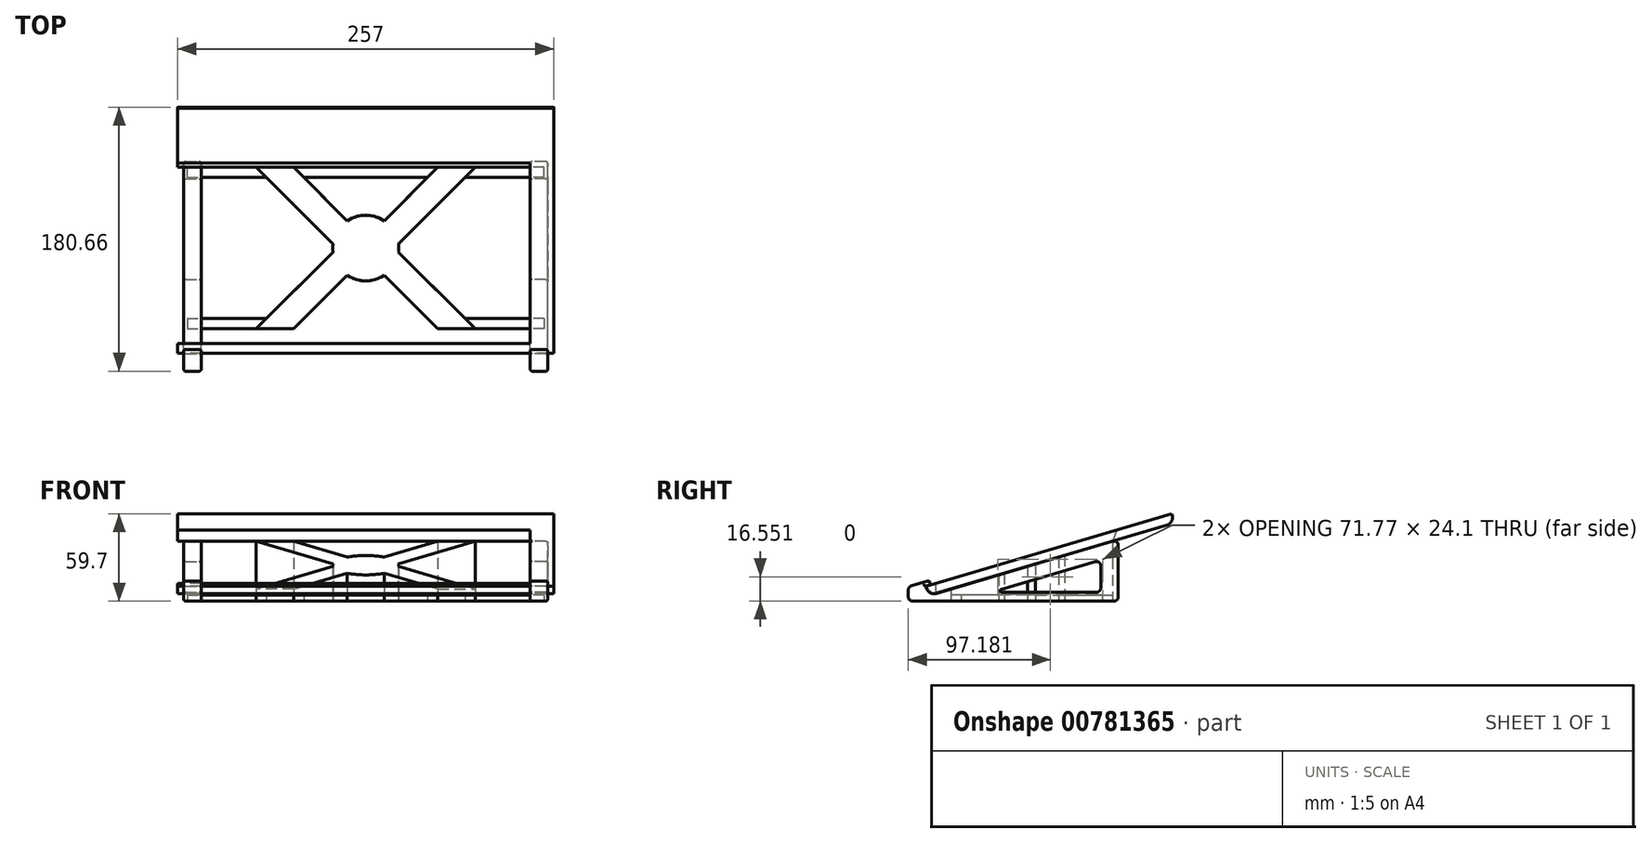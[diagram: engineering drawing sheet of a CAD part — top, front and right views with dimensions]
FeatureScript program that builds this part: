
annotation { "Feature Type Name" : "Feature", "Feature Type Description" : "" }
export const myFeature = defineFeature(function(context is Context, id is Id, definition is map)
    precondition{}
    {
        {
            var Q0;
            Q0=qCreatedBy(makeId("Right.planeOp"),FACE);
            var sketch = newSketch(context, id + "F0", { "sketchPlane" : qUnion([Q0])});
            skLineSegment(sketch, "E0", {"start": v(0, 10) * mm, "end": v(167.8, 59.7) * mm});
            skLineSegment(sketch, "E1", {"start": v(167.8, 59.7) * mm, "end": v(168.16, 58.46) * mm});
            skLineSegment(sketch, "E2", {"start": v(164.65, 52) * mm, "end": v(6.83, 5.24) * mm});
            skLineSegment(sketch, "E3", {"start": v(0.37, 8.75) * mm, "end": v(0, 10) * mm});
            skPoint(sketch, "E4.visualSharp", {"position": v(1.85, 3.77) * mm});
            skArc(sketch, "E4.filletArc", {"start": v(0.37, 8.75) * mm, "mid": v(2.87, 5.66) * mm, "end": v(6.83, 5.24) * mm});
            skPoint(sketch, "E5.visualSharp", {"position": v(169.64, 53.47) * mm});
            skArc(sketch, "E5.filletArc", {"start": v(164.65, 52) * mm, "mid": v(167.75, 54.5) * mm, "end": v(168.16, 58.46) * mm});
            skLineSegment(sketch, "E6", {"start": v(0, 0) * mm, "end": v(83.66, 0) * mm, "construction": true});
            skSolve(sketch);
        }
        {
            var Q0;
            Q0=makeQuery(id+"F0.imprint","IMPRINT",FACE,{"disambiguationData":[TD([[makeQuery(id+"F0.imprint","IMPRINT",EDGE,{"derivedFrom":sQuery(id+"F0.wireOp",EDGE,"E0")}),-1.0]])]});
            extrude(context, id + "F1", {"entities" : qUnion([Q0]), "endBound" : BoundingType.SYMMETRIC, "depth" : 257 * mm, "offsetDistance" : 25 * mm});
        }
        {
            var Q0;
            Q0=makeQuery(id+"F1.opExtrude","CAP_FACE",FACE,{"disambiguationData":[OSD([sQuery(id+"F0.wireOp",EDGE,"E0"),sQuery(id+"F0.wireOp",EDGE,"E1"),sQuery(id+"F0.wireOp",EDGE,"E2"),sQuery(id+"F0.wireOp",EDGE,"E3"),sQuery(id+"F0.wireOp",EDGE,"E4.filletArc"),sQuery(id+"F0.wireOp",EDGE,"E5.filletArc")])],"isStart":false});
            cPlane(context, id + "F2", {"entities" : qUnion([Q0]), "cplaneType" : CPlaneType.OFFSET, "offset" : 16 * mm, "oppositeDirection" : true, "width" : 150 * mm, "height" : 150 * mm});
        }
        {
            var Q0;
            Q0=qCreatedBy(id+"F2.planeOp",FACE);
            var sketch = newSketch(context, id + "F3", { "sketchPlane" : qUnion([Q0])});
            skLineSegment(sketch, "E7", {"start": v(6.74, 5.22) * mm, "end": v(127.43, 40.97) * mm});
            skLineSegment(sketch, "E8", {"start": v(131.29, 38.1) * mm, "end": v(131.29, 3) * mm});
            skLineSegment(sketch, "E9", {"start": v(-9.28, 0) * mm, "end": v(128.29, 0) * mm});
            skLineSegment(sketch, "E10.0", {"start": v(167.8, 59.7) * mm, "end": v(168.16, 58.46) * mm, "construction": true});
            skLineSegment(sketch, "E11", {"start": v(131.29, 42.1) * mm, "end": v(169.64, 53.47) * mm, "construction": true});
            skLineSegment(sketch, "E12", {"start": v(169.64, 53.47) * mm, "end": v(168.16, 58.46) * mm, "construction": true});
            skArc(sketch, "E13", {"start": v(6.74, 5.22) * mm, "mid": v(2.7, 5.64) * mm, "end": v(0.15, 8.8) * mm});
            skLineSegment(sketch, "E14", {"start": v(-0.28, 10.23) * mm, "end": v(0.15, 8.8) * mm});
            skLineSegment(sketch, "E15.0", {"start": v(0, 10) * mm, "end": v(167.8, 59.7) * mm, "construction": true});
            skLineSegment(sketch, "E16", {"start": v(-0.28, 10.23) * mm, "end": v(1.64, 10.8) * mm});
            skLineSegment(sketch, "E17", {"start": v(-12.28, 7.56) * mm, "end": v(-12.28, 3) * mm});
            skLineSegment(sketch, "E18", {"start": v(0.79, 13.68) * mm, "end": v(-10.13, 10.44) * mm});
            skArc(sketch, "E19", {"start": v(0.79, 13.68) * mm, "mid": v(2.65, 12.66) * mm, "end": v(1.64, 10.8) * mm});
            skLineSegment(sketch, "E20", {"start": v(51.2, 7.96) * mm, "end": v(115.43, 26.98) * mm});
            skLineSegment(sketch, "E21", {"start": v(119.29, 24.1) * mm, "end": v(119.29, 9) * mm});
            skLineSegment(sketch, "E22", {"start": v(116.29, 6) * mm, "end": v(51.49, 6) * mm});
            skPoint(sketch, "E23.visualSharp", {"position": v(44.6, 6) * mm});
            skArc(sketch, "E23.filletArc", {"start": v(51.2, 7.96) * mm, "mid": v(50.5, 6.86) * mm, "end": v(51.49, 6) * mm});
            skPoint(sketch, "E24.visualSharp", {"position": v(119.29, 28.13) * mm});
            skArc(sketch, "E24.filletArc", {"start": v(119.29, 24.1) * mm, "mid": v(118.08, 26.51) * mm, "end": v(115.43, 26.98) * mm});
            skPoint(sketch, "E25.visualSharp", {"position": v(119.29, 6) * mm});
            skArc(sketch, "E25.filletArc", {"start": v(116.29, 6) * mm, "mid": v(118.4, 6.88) * mm, "end": v(119.29, 9) * mm});
            skPoint(sketch, "E26.visualSharp", {"position": v(131.29, 0) * mm});
            skArc(sketch, "E26.filletArc", {"start": v(128.29, 0) * mm, "mid": v(130.4, 0.88) * mm, "end": v(131.29, 3) * mm});
            skPoint(sketch, "E27.visualSharp", {"position": v(131.29, 42.1) * mm});
            skArc(sketch, "E27.filletArc", {"start": v(131.29, 38.1) * mm, "mid": v(130.08, 40.5) * mm, "end": v(127.43, 40.97) * mm});
            skPoint(sketch, "E28.visualSharp", {"position": v(-12.28, 0) * mm});
            skArc(sketch, "E28.filletArc", {"start": v(-12.28, 3) * mm, "mid": v(-11.4, 0.88) * mm, "end": v(-9.28, 0) * mm});
            skArc(sketch, "E29", {"start": v(-10.13, 10.44) * mm, "mid": v(-11.68, 9.36) * mm, "end": v(-12.28, 7.56) * mm});
            skSolve(sketch);
        }
        {
            var Q0;
            Q0=makeQuery(id+"F3.imprint","IMPRINT",FACE,{"disambiguationData":[TD([[makeQuery(id+"F3.imprint","IMPRINT",EDGE,{"derivedFrom":sQuery(id+"F3.wireOp",EDGE,"E7")}),-1.0]])]});
            extrude(context, id + "F4", {"entities" : qUnion([Q0]), "depth" : 12 * mm, "offsetDistance" : 25 * mm});
        }
        {
            var Q0;
            Q0=makeQuery(id+"F4.opExtrude","CAP_FACE",FACE,{"disambiguationData":[OSD([sQuery(id+"F3.wireOp",EDGE,"E7"),sQuery(id+"F3.wireOp",EDGE,"E8"),sQuery(id+"F3.wireOp",EDGE,"E9"),sQuery(id+"F3.wireOp",EDGE,"E13"),sQuery(id+"F3.wireOp",EDGE,"E14"),sQuery(id+"F3.wireOp",EDGE,"E16"),sQuery(id+"F3.wireOp",EDGE,"E17"),sQuery(id+"F3.wireOp",EDGE,"E18"),sQuery(id+"F3.wireOp",EDGE,"E19"),sQuery(id+"F3.wireOp",EDGE,"E20"),sQuery(id+"F3.wireOp",EDGE,"E21"),sQuery(id+"F3.wireOp",EDGE,"E22"),sQuery(id+"F3.wireOp",EDGE,"E23.filletArc"),sQuery(id+"F3.wireOp",EDGE,"E24.filletArc"),sQuery(id+"F3.wireOp",EDGE,"E25.filletArc"),sQuery(id+"F3.wireOp",EDGE,"E26.filletArc"),sQuery(id+"F3.wireOp",EDGE,"E27.filletArc"),sQuery(id+"F3.wireOp",EDGE,"E28.filletArc"),sQuery(id+"F3.wireOp",EDGE,"E29")])],"isStart":false});
            var Q1;
            Q1=makeQuery(id+"F4.opExtrude","CAP_FACE",FACE,{"disambiguationData":[OSD([sQuery(id+"F3.wireOp",EDGE,"E7"),sQuery(id+"F3.wireOp",EDGE,"E8"),sQuery(id+"F3.wireOp",EDGE,"E9"),sQuery(id+"F3.wireOp",EDGE,"E13"),sQuery(id+"F3.wireOp",EDGE,"E14"),sQuery(id+"F3.wireOp",EDGE,"E16"),sQuery(id+"F3.wireOp",EDGE,"E17"),sQuery(id+"F3.wireOp",EDGE,"E18"),sQuery(id+"F3.wireOp",EDGE,"E19"),sQuery(id+"F3.wireOp",EDGE,"E20"),sQuery(id+"F3.wireOp",EDGE,"E21"),sQuery(id+"F3.wireOp",EDGE,"E22"),sQuery(id+"F3.wireOp",EDGE,"E23.filletArc"),sQuery(id+"F3.wireOp",EDGE,"E24.filletArc"),sQuery(id+"F3.wireOp",EDGE,"E25.filletArc"),sQuery(id+"F3.wireOp",EDGE,"E26.filletArc"),sQuery(id+"F3.wireOp",EDGE,"E27.filletArc"),sQuery(id+"F3.wireOp",EDGE,"E28.filletArc"),sQuery(id+"F3.wireOp",EDGE,"E29")])],"isStart":true});
            fillet(context, id + "F5", {"entities" : qUnion([Q0, Q1]), "radius" : 1.5 * mm, "tangentPropagation" : true, "allowEdgeOverflow" : false});
        }
        {
            var Q0;
            Q0=makeQuery(id+"F4.opExtrude","SWEPT_BODY",BODY,{"disambiguationData":[OSD([sQuery(id+"F3.wireOp",EDGE,"E7"),sQuery(id+"F3.wireOp",EDGE,"E8"),sQuery(id+"F3.wireOp",EDGE,"E9"),sQuery(id+"F3.wireOp",EDGE,"E13"),sQuery(id+"F3.wireOp",EDGE,"E14"),sQuery(id+"F3.wireOp",EDGE,"E16"),sQuery(id+"F3.wireOp",EDGE,"E17"),sQuery(id+"F3.wireOp",EDGE,"E18"),sQuery(id+"F3.wireOp",EDGE,"E19"),sQuery(id+"F3.wireOp",EDGE,"E20"),sQuery(id+"F3.wireOp",EDGE,"E21"),sQuery(id+"F3.wireOp",EDGE,"E22"),sQuery(id+"F3.wireOp",EDGE,"E23.filletArc"),sQuery(id+"F3.wireOp",EDGE,"E24.filletArc"),sQuery(id+"F3.wireOp",EDGE,"E25.filletArc"),sQuery(id+"F3.wireOp",EDGE,"E26.filletArc"),sQuery(id+"F3.wireOp",EDGE,"E27.filletArc"),sQuery(id+"F3.wireOp",EDGE,"E28.filletArc"),sQuery(id+"F3.wireOp",EDGE,"E29")])]});
            var Q1;
            Q1=qCreatedBy(makeId("Right.planeOp"),FACE);
            mirror(context, id + "F6", {"entities" : qUnion([Q0]), "mirrorPlane" : qUnion([Q1])});
        }
        {
            var Q0;
            Q0=makeQuery(id+"F4.opExtrude","SWEPT_FACE",FACE,{"disambiguationData":[OSD([sQuery(id+"F3.wireOp",EDGE,"E9")])]});
            var sketch = newSketch(context, id + "F7", { "sketchPlane" : qUnion([Q0])});
            skLineSegment(sketch, "E30.0.0", {"start": v(-114, -119.29) * mm, "end": v(-123, -119.29) * mm, "construction": true});
            skLineSegment(sketch, "E30.0.2", {"start": v(-123, -119.29) * mm, "end": v(-114, -119.29) * mm, "construction": true});
            skLineSegment(sketch, "E31.0", {"start": v(-123, -128.29) * mm, "end": v(-123, 9.28) * mm, "construction": true});
            skLineSegment(sketch, "E32.0", {"start": v(-114, 9.28) * mm, "end": v(-114, -128.29) * mm, "construction": true});
            skLineSegment(sketch, "E33.0", {"start": v(-123, -128.29) * mm, "end": v(-114, -128.29) * mm, "construction": true});
            skLineSegment(sketch, "E34", {"start": v(0, 0) * mm, "end": v(0, -136.16) * mm, "construction": true});
            skLineSegment(sketch, "E35.bottom", {"start": v(-122, -120.29) * mm, "end": v(0, -120.29) * mm});
            skLineSegment(sketch, "E35.top", {"start": v(-122, -127.29) * mm, "end": v(0, -127.29) * mm});
            skLineSegment(sketch, "E35.left", {"start": v(-122, -120.29) * mm, "end": v(-122, -127.29) * mm});
            skLineSegment(sketch, "E36.MirrorCS", {"start": v(-122, -23.74) * mm, "end": v(-122, -16.74) * mm});
            skLineSegment(sketch, "E37.MirrorCS", {"start": v(-122, -23.74) * mm, "end": v(0, -23.74) * mm});
            skLineSegment(sketch, "E38.MirrorCS", {"start": v(-122, -16.74) * mm, "end": v(0, -16.74) * mm});
            skLineSegment(sketch, "E39.0", {"start": v(-123, -6.74) * mm, "end": v(-114, -6.74) * mm, "construction": true});
            skLineSegment(sketch, "E40", {"start": v(-57, -23.74) * mm, "end": v(-57, -120.29) * mm, "construction": true});
            skLineSegment(sketch, "E41", {"start": v(-114, -72.01) * mm, "end": v(0, -72.01) * mm, "construction": true});
            skPoint(sketch, "E42", {"position": v(-57, -72.01) * mm});
            skCircle(sketch, "E43", {"center": v(0, -72.01) * mm, "radius": 22.5 * mm});
            skLineSegment(sketch, "E44", {"start": v(0, -72.01) * mm, "end": v(-48.28, -23.74) * mm, "construction": true});
            skLineSegment(sketch, "E45", {"start": v(-12.62, -53.38) * mm, "end": v(-49.26, -16.74) * mm});
            skLineSegment(sketch, "E46.MirrorCS", {"start": v(-12.62, -90.64) * mm, "end": v(-49.26, -127.29) * mm});
            skLineSegment(sketch, "E47", {"start": v(-22.33, -69.25) * mm, "end": v(-74.85, -16.74) * mm});
            skLineSegment(sketch, "E48.MirrorCS", {"start": v(-22.33, -74.77) * mm, "end": v(-74.85, -127.29) * mm});
            skLineSegment(sketch, "E49.MirrorCS", {"start": v(122, -16.74) * mm, "end": v(0, -16.74) * mm});
            skLineSegment(sketch, "E50.MirrorCS", {"start": v(122, -23.74) * mm, "end": v(0, -23.74) * mm});
            skLineSegment(sketch, "E51.MirrorCS", {"start": v(122, -120.29) * mm, "end": v(0, -120.29) * mm});
            skLineSegment(sketch, "E52.MirrorCS", {"start": v(122, -127.29) * mm, "end": v(0, -127.29) * mm});
            skLineSegment(sketch, "E53.MirrorCS", {"start": v(122, -23.74) * mm, "end": v(122, -16.74) * mm});
            skLineSegment(sketch, "E54.MirrorCS", {"start": v(122, -120.29) * mm, "end": v(122, -127.29) * mm});
            skLineSegment(sketch, "E55.MirrorCS", {"start": v(12.62, -53.38) * mm, "end": v(49.26, -16.74) * mm});
            skLineSegment(sketch, "E56.MirrorCS", {"start": v(22.33, -69.25) * mm, "end": v(74.85, -16.74) * mm});
            skLineSegment(sketch, "E57.MirrorCS", {"start": v(22.33, -74.77) * mm, "end": v(74.85, -127.29) * mm});
            skLineSegment(sketch, "E58.MirrorCS", {"start": v(12.62, -90.64) * mm, "end": v(49.26, -127.29) * mm});
            skPoint(sketch, "E59.orphan", {"position": v(-67.85, -23.74) * mm});
            skPoint(sketch, "E60.orphan", {"position": v(-42.26, -23.74) * mm});
            skPoint(sketch, "E61.orphan", {"position": v(-67.85, -120.29) * mm});
            skPoint(sketch, "E62.orphan", {"position": v(-42.26, -120.29) * mm});
            skPoint(sketch, "E63.orphan", {"position": v(42.26, -120.29) * mm});
            skPoint(sketch, "E64.orphan", {"position": v(67.85, -120.29) * mm});
            skPoint(sketch, "E65.orphan", {"position": v(67.85, -23.74) * mm});
            skPoint(sketch, "E66.orphan", {"position": v(42.26, -23.74) * mm});
            skSolve(sketch);
        }
        {
            var Q0;
            {var subQ0=sQuery(id+"F7.wireOp",EDGE,"E57.MirrorCS");Q0=makeQuery(id+"F7.imprint","IMPRINT",FACE,{"disambiguationData":[TD([[makeQuery(id+"F7.imprint","IMPRINT",EDGE,{"derivedFrom":subQ0}),-1.0]])]});}
            var Q1;
            {var subQ0=sQuery(id+"F7.wireOp",EDGE,"E46.MirrorCS");Q1=makeQuery(id+"F7.imprint","IMPRINT",FACE,{"disambiguationData":[TD([[makeQuery(id+"F7.imprint","IMPRINT",EDGE,{"derivedFrom":subQ0}),-1.0]])]});}
            var Q2;
            {var subQ0=sQuery(id+"F7.wireOp",EDGE,"E35.top");Q2=makeQuery(id+"F7.imprint","IMPRINT",FACE,{"disambiguationData":[TD([[makeQuery(id+"F7.imprint","IMPRINT",EDGE,{"derivedFrom":subQ0}),1.0]])]});}
            var Q3;
            {var subQ0=sQuery(id+"F7.wireOp",EDGE,"E43");var subQ4=makeQuery(id+"F7.imprint","INTERSECT",VERTEX,{"derivedFrom":[subQ0,sQuery(id+"F7.wireOp",EDGE,"E45")]});Q3=makeQuery(id+"F7.imprint","IMPRINT",FACE,{"disambiguationData":[TD([[makeQuery(id+"F7.imprint","IMPRINT",EDGE,{"disambiguationData":[TD([[subQ4,1.0]])],"derivedFrom":subQ0}),1.0]])]});}
            var Q4;
            {var subQ0=sQuery(id+"F7.wireOp",EDGE,"E55.MirrorCS");Q4=makeQuery(id+"F7.imprint","IMPRINT",FACE,{"disambiguationData":[TD([[makeQuery(id+"F7.imprint","IMPRINT",EDGE,{"derivedFrom":subQ0}),-1.0]])]});}
            var Q5;
            {var subQ0=sQuery(id+"F7.wireOp",EDGE,"E45");Q5=makeQuery(id+"F7.imprint","IMPRINT",FACE,{"disambiguationData":[TD([[makeQuery(id+"F7.imprint","IMPRINT",EDGE,{"derivedFrom":subQ0}),1.0]])]});}
            var Q6;
            {var subQ5=sQuery(id+"F7.wireOp",EDGE,"E36.MirrorCS");Q6=makeQuery(id+"F7.imprint","IMPRINT",FACE,{"disambiguationData":[TD([[makeQuery(id+"F7.imprint","IMPRINT",EDGE,{"derivedFrom":subQ5}),-1.0]])]});}
            var Q7;
            {var subQ0=sQuery(id+"F7.wireOp",EDGE,"E53.MirrorCS");Q7=makeQuery(id+"F7.imprint","IMPRINT",FACE,{"disambiguationData":[TD([[makeQuery(id+"F7.imprint","IMPRINT",EDGE,{"derivedFrom":subQ0}),1.0]])]});}
            var Q8;
            {var subQ0=sQuery(id+"F7.wireOp",EDGE,"E54.MirrorCS");Q8=makeQuery(id+"F7.imprint","IMPRINT",FACE,{"disambiguationData":[TD([[makeQuery(id+"F7.imprint","IMPRINT",EDGE,{"derivedFrom":subQ0}),-1.0]])]});}
            var Q9;
            {var subQ0=sQuery(id+"F7.wireOp",EDGE,"E56.MirrorCS");var subQ1=sQuery(id+"F7.wireOp",EDGE,"E49.MirrorCS");var subQ2=makeQuery(id+"F7.imprint","INTERSECT",VERTEX,{"derivedFrom":[subQ1,subQ0]});Q9=makeQuery(id+"F7.imprint","IMPRINT",FACE,{"disambiguationData":[TD([[makeQuery(id+"F7.imprint","IMPRINT",EDGE,{"disambiguationData":[TD([[subQ2,1.0]])],"derivedFrom":subQ0}),-1.0]])]});}
            var Q10;
            {var subQ0=sQuery(id+"F7.wireOp",EDGE,"E57.MirrorCS");var subQ6=sQuery(id+"F7.wireOp",EDGE,"E52.MirrorCS");var subQ7=makeQuery(id+"F7.imprint","INTERSECT",VERTEX,{"derivedFrom":[subQ6,subQ0]});Q10=makeQuery(id+"F7.imprint","IMPRINT",FACE,{"disambiguationData":[TD([[makeQuery(id+"F7.imprint","IMPRINT",EDGE,{"disambiguationData":[TD([[subQ7,1.0]])],"derivedFrom":subQ0}),1.0]])]});}
            var Q11;
            {var subQ0=sQuery(id+"F7.wireOp",EDGE,"E51.MirrorCS");var subQ1=sQuery(id+"F7.wireOp",EDGE,"E35.bottom");var subQ2=makeQuery(id+"F7.imprint","INTERSECT",VERTEX,{"derivedFrom":[subQ1,subQ0]});Q11=makeQuery(id+"F7.imprint","IMPRINT",FACE,{"disambiguationData":[TD([[makeQuery(id+"F7.imprint","IMPRINT",EDGE,{"disambiguationData":[TD([[subQ2,1.0]])],"derivedFrom":subQ1}),-1.0]])]});}
            var Q12;
            Q12=makeQuery(id+"F6.opPattern","COPY",FACE,{"derivedFrom":makeQuery(id+"F4.opExtrude","SWEPT_FACE",FACE,{"disambiguationData":[OSD([sQuery(id+"F3.wireOp",EDGE,"E22")])]}),"instanceName":"1"});
            extrude(context, id + "F8", {"entities" : qUnion([Q0, Q1, Q2, Q3, Q4, Q5, Q6, Q7, Q8, Q9, Q10, Q11]), "oppositeDirection" : true, "depth" : 4 * mm, "endBoundEntityFace" : qUnion([Q12]), "offsetDistance" : 25 * mm});
        }
        {
            var Q0;
            Q0=makeQuery(id+"F4.opExtrude","SWEPT_EDGE",EDGE,{"disambiguationData":[OSD([sQuery(id+"F3.wireOp",EDGE,"E7"),sQuery(id+"F3.wireOp",EDGE,"E27.filletArc")])]});
            cPlane(context, id + "F9", {"entities" : qUnion([Q0]), "cplaneType" : CPlaneType.LINE_ANGLE, "offset" : 25 * mm, "angle" : 90 * degree, "width" : 150 * mm, "height" : 150 * mm});
        }
        {
            var Q0;
            {var subQ0=sQuery(id+"F7.wireOp",EDGE,"E47");var subQ1=sQuery(id+"F7.wireOp",EDGE,"E37.MirrorCS");var subQ2=makeQuery(id+"F7.imprint","INTERSECT",VERTEX,{"derivedFrom":[subQ1,subQ0]});Q0=makeQuery(id+"F7.imprint","IMPRINT",FACE,{"disambiguationData":[TD([[makeQuery(id+"F7.imprint","IMPRINT",EDGE,{"disambiguationData":[TD([[subQ2,-1.0]])],"derivedFrom":subQ1}),-1.0]])]});}
            var Q1;
            {var subQ0=sQuery(id+"F7.wireOp",EDGE,"E55.MirrorCS");var subQ1=sQuery(id+"F7.wireOp",EDGE,"E43");var subQ2=makeQuery(id+"F7.imprint","INTERSECT",VERTEX,{"derivedFrom":[subQ1,subQ0]});Q1=makeQuery(id+"F7.imprint","IMPRINT",FACE,{"disambiguationData":[TD([[makeQuery(id+"F7.imprint","IMPRINT",EDGE,{"disambiguationData":[TD([[subQ2,1.0]])],"derivedFrom":subQ1}),-1.0]])]});}
            var Q2;
            {var subQ0=sQuery(id+"F7.wireOp",EDGE,"E43");var subQ4=makeQuery(id+"F7.imprint","INTERSECT",VERTEX,{"derivedFrom":[subQ0,sQuery(id+"F7.wireOp",EDGE,"E45")]});Q2=makeQuery(id+"F7.imprint","IMPRINT",FACE,{"disambiguationData":[TD([[makeQuery(id+"F7.imprint","IMPRINT",EDGE,{"disambiguationData":[TD([[subQ4,1.0]])],"derivedFrom":subQ0}),1.0]])]});}
            var Q3;
            {var subQ0=sQuery(id+"F7.wireOp",EDGE,"E57.MirrorCS");var subQ1=sQuery(id+"F7.wireOp",EDGE,"E43");var subQ2=makeQuery(id+"F7.imprint","INTERSECT",VERTEX,{"derivedFrom":[subQ1,subQ0]});Q3=makeQuery(id+"F7.imprint","IMPRINT",FACE,{"disambiguationData":[TD([[makeQuery(id+"F7.imprint","IMPRINT",EDGE,{"disambiguationData":[TD([[subQ2,1.0]])],"derivedFrom":subQ1}),-1.0]])]});}
            var Q4;
            {var subQ0=sQuery(id+"F7.wireOp",EDGE,"E48.MirrorCS");var subQ1=sQuery(id+"F7.wireOp",EDGE,"E35.bottom");var subQ2=makeQuery(id+"F7.imprint","INTERSECT",VERTEX,{"derivedFrom":[subQ1,subQ0]});Q4=makeQuery(id+"F7.imprint","IMPRINT",FACE,{"disambiguationData":[TD([[makeQuery(id+"F7.imprint","IMPRINT",EDGE,{"disambiguationData":[TD([[subQ2,-1.0]])],"derivedFrom":subQ1}),1.0]])]});}
            var Q5;
            {var subQ0=sQuery(id+"F7.wireOp",EDGE,"E57.MirrorCS");var subQ1=sQuery(id+"F7.wireOp",EDGE,"E51.MirrorCS");var subQ2=makeQuery(id+"F7.imprint","INTERSECT",VERTEX,{"derivedFrom":[subQ1,subQ0]});Q5=makeQuery(id+"F7.imprint","IMPRINT",FACE,{"disambiguationData":[TD([[makeQuery(id+"F7.imprint","IMPRINT",EDGE,{"disambiguationData":[TD([[subQ2,-1.0]])],"derivedFrom":subQ1}),1.0]])]});}
            var Q6;
            {var subQ0=sQuery(id+"F7.wireOp",EDGE,"E48.MirrorCS");var subQ1=sQuery(id+"F7.wireOp",EDGE,"E35.bottom");var subQ2=makeQuery(id+"F7.imprint","INTERSECT",VERTEX,{"derivedFrom":[subQ1,subQ0]});Q6=makeQuery(id+"F7.imprint","IMPRINT",FACE,{"disambiguationData":[TD([[makeQuery(id+"F7.imprint","IMPRINT",EDGE,{"disambiguationData":[TD([[subQ2,-1.0]])],"derivedFrom":subQ1}),-1.0]])]});}
            var Q7;
            {var subQ0=sQuery(id+"F7.wireOp",EDGE,"E47");var subQ1=sQuery(id+"F7.wireOp",EDGE,"E37.MirrorCS");var subQ2=makeQuery(id+"F7.imprint","INTERSECT",VERTEX,{"derivedFrom":[subQ1,subQ0]});Q7=makeQuery(id+"F7.imprint","IMPRINT",FACE,{"disambiguationData":[TD([[makeQuery(id+"F7.imprint","IMPRINT",EDGE,{"disambiguationData":[TD([[subQ2,-1.0]])],"derivedFrom":subQ1}),1.0]])]});}
            var Q8;
            {var subQ0=sQuery(id+"F7.wireOp",EDGE,"E55.MirrorCS");var subQ1=sQuery(id+"F7.wireOp",EDGE,"E49.MirrorCS");var subQ2=makeQuery(id+"F7.imprint","INTERSECT",VERTEX,{"derivedFrom":[subQ1,subQ0]});Q8=makeQuery(id+"F7.imprint","IMPRINT",FACE,{"disambiguationData":[TD([[makeQuery(id+"F7.imprint","IMPRINT",EDGE,{"disambiguationData":[TD([[subQ2,1.0]])],"derivedFrom":subQ1}),1.0]])]});}
            var Q9;
            Q9=qCreatedBy(id+"F9.planeOp",FACE);
            extrude(context, id + "F10", {"entities" : qUnion([Q0, Q1, Q2, Q3, Q4, Q5, Q6, Q7, Q8]), "endBound" : BoundingType.UP_TO_SURFACE, "oppositeDirection" : true, "depth" : 35.2 * mm, "endBoundEntityFace" : qUnion([Q9]), "offsetDistance" : 25 * mm});
        }
        {
            var Q0;
            Q0=makeQuery(id+"F3.imprint","IMPRINT",FACE,{"disambiguationData":[TD([[makeQuery(id+"F3.imprint","IMPRINT",EDGE,{"derivedFrom":sQuery(id+"F3.wireOp",EDGE,"E7")}),-1.0]])]});
            var sketch = newSketch(context, id + "F11", { "sketchPlane" : qUnion([Q0])});
            skLineSegment(sketch, "E67.0", {"start": v(6.74, 5.22) * mm, "end": v(127.43, 40.97) * mm});
            skLineSegment(sketch, "E68", {"start": v(6.74, 5.22) * mm, "end": v(6.74, 57.2) * mm});
            skLineSegment(sketch, "E69", {"start": v(6.74, 57.2) * mm, "end": v(133.2, 57.2) * mm});
            skLineSegment(sketch, "E70", {"start": v(133.2, 57.2) * mm, "end": v(127.43, 40.97) * mm});
            skSolve(sketch);
        }
        {
            var Q0;
            Q0=makeQuery(id+"F11.imprint","IMPRINT",FACE,{"disambiguationData":[TD([[makeQuery(id+"F11.imprint","IMPRINT",EDGE,{"derivedFrom":sQuery(id+"F11.wireOp",EDGE,"E67.0")}),1.0]])]});
            extrude(context, id + "F12", {"entities" : qUnion([Q0]), "operationType" : NewBodyOperationType.REMOVE, "endBound" : BoundingType.THROUGH_ALL, "oppositeDirection" : true, "depth" : 25 * mm, "offsetDistance" : 25 * mm});
        }
    });
